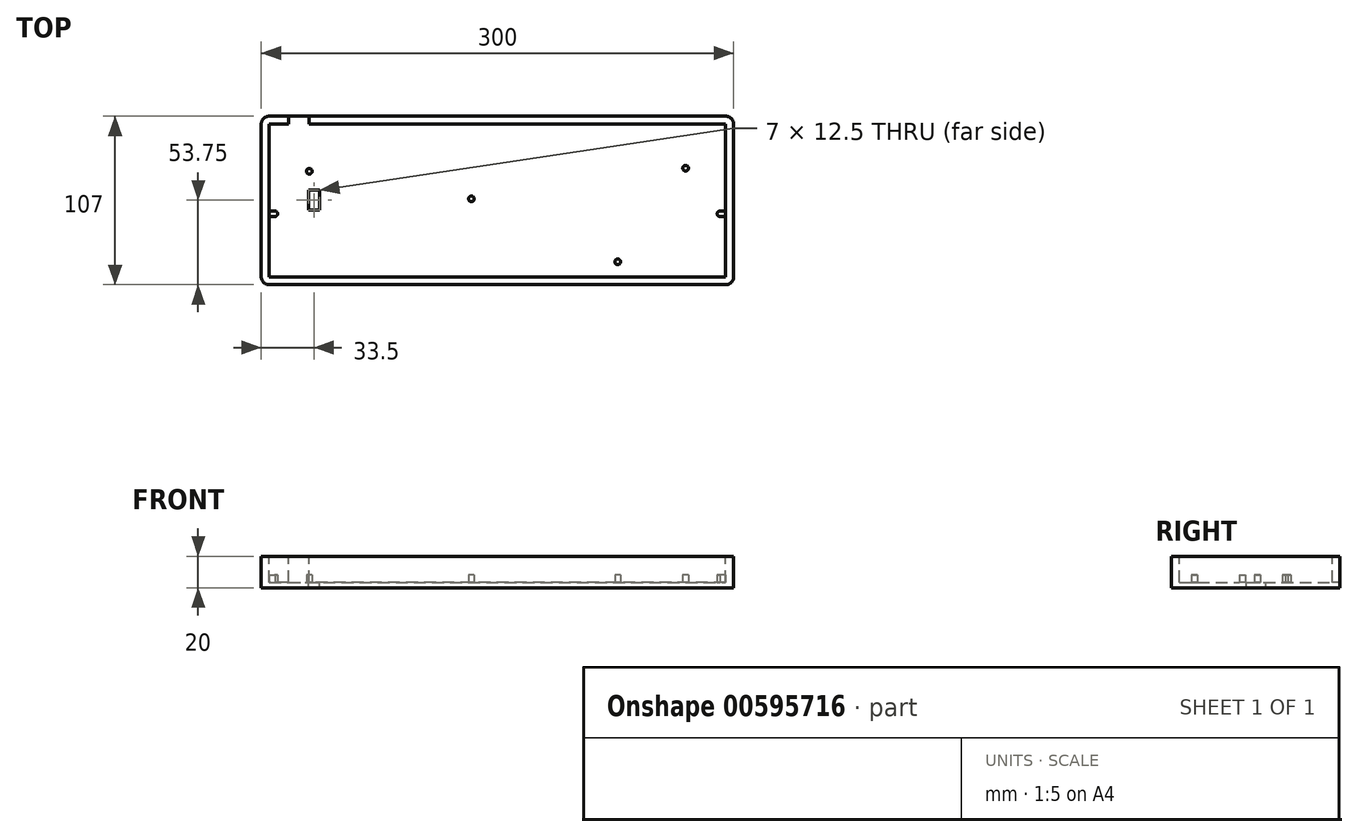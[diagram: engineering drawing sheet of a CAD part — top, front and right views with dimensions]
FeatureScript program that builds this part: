
annotation { "Feature Type Name" : "Feature", "Feature Type Description" : "" }
export const myFeature = defineFeature(function(context is Context, id is Id, definition is map)
    precondition{}
    {
        {
            var Q0;
            Q0=qCreatedBy(makeId("Top.planeOp"),FACE);
            var sketch = newSketch(context, id + "F0", { "sketchPlane" : qUnion([Q0])});
            skLineSegment(sketch, "E0.bottom", {"start": v(0, 0) * mm, "end": v(300, 0) * mm});
            skLineSegment(sketch, "E0.top", {"start": v(0, 107) * mm, "end": v(300, 107) * mm});
            skLineSegment(sketch, "E0.left", {"start": v(0, 0) * mm, "end": v(0, 107) * mm});
            skLineSegment(sketch, "E0.right", {"start": v(300, 0) * mm, "end": v(300, 107) * mm});
            skSolve(sketch);
        }
        {
            var Q0;
            Q0 = qSketchRegion(id + "F0", true);
            extrude(context, id + "F1", {"entities" : qUnion([Q0]), "depth" : 20 * mm, "offsetDistance" : 25 * mm});
        }
        {
            var Q0;
            Q0=makeQuery(id+"F1.opExtrude","SWEPT_EDGE",EDGE,{"disambiguationData":[OSD([sQuery(id+"F0.wireOp",EDGE,"E0.top"),sQuery(id+"F0.wireOp",EDGE,"E0.left")])]});
            var Q1;
            Q1=makeQuery(id+"F1.opExtrude","SWEPT_EDGE",EDGE,{"disambiguationData":[OSD([sQuery(id+"F0.wireOp",EDGE,"E0.bottom"),sQuery(id+"F0.wireOp",EDGE,"E0.left")])]});
            var Q2;
            Q2=makeQuery(id+"F1.opExtrude","SWEPT_EDGE",EDGE,{"disambiguationData":[OSD([sQuery(id+"F0.wireOp",EDGE,"E0.bottom"),sQuery(id+"F0.wireOp",EDGE,"E0.right")])]});
            var Q3;
            Q3=makeQuery(id+"F1.opExtrude","SWEPT_EDGE",EDGE,{"disambiguationData":[OSD([sQuery(id+"F0.wireOp",EDGE,"E0.top"),sQuery(id+"F0.wireOp",EDGE,"E0.right")])]});
            fillet(context, id + "F2", {"entities" : qUnion([Q0, Q1, Q2, Q3]), "radius" : 5 * mm, "tangentPropagation" : true, "allowEdgeOverflow" : false});
        }
        {
            var Q0;
            Q0=makeQuery(id+"F1.opExtrude","CAP_FACE",FACE,{"disambiguationData":[OSD([sQuery(id+"F0.wireOp",EDGE,"E0.bottom"),sQuery(id+"F0.wireOp",EDGE,"E0.top"),sQuery(id+"F0.wireOp",EDGE,"E0.left"),sQuery(id+"F0.wireOp",EDGE,"E0.right")])],"isStart":false});
            var sketch = newSketch(context, id + "F3", { "sketchPlane" : qUnion([Q0])});
            skLineSegment(sketch, "E1", {"start": v(5, 102) * mm, "end": v(5, 5) * mm});
            skLineSegment(sketch, "E2", {"start": v(5, 5) * mm, "end": v(295, 5) * mm});
            skLineSegment(sketch, "E3", {"start": v(295, 5) * mm, "end": v(295, 102) * mm});
            skLineSegment(sketch, "E4", {"start": v(295, 102) * mm, "end": v(5, 102) * mm});
            skLineSegment(sketch, "E5", {"start": v(17.5, 102) * mm, "end": v(17.5, 107) * mm});
            skLineSegment(sketch, "E6", {"start": v(17.5, 107) * mm, "end": v(30.5, 107) * mm});
            skLineSegment(sketch, "E7", {"start": v(30.5, 107) * mm, "end": v(30.5, 102) * mm});
            skSolve(sketch);
        }
        {
            var Q0;
            Q0 = qSketchRegion(id + "F3", true);
            var Q1;
            Q1=makeQuery(id+"F1.opExtrude","CAP_FACE",FACE,{"disambiguationData":[OSD([sQuery(id+"F0.wireOp",EDGE,"E0.bottom"),sQuery(id+"F0.wireOp",EDGE,"E0.top"),sQuery(id+"F0.wireOp",EDGE,"E0.left"),sQuery(id+"F0.wireOp",EDGE,"E0.right")])],"isStart":true});
            extrude(context, id + "F4", {"entities" : qUnion([Q0, Q1]), "operationType" : NewBodyOperationType.REMOVE, "oppositeDirection" : true, "depth" : 16.5 * mm, "offsetDistance" : 25 * mm});
        }
        {
            var Q0;
            Q0=makeQuery(id+"F4.boolean.opBoolean","COPY",FACE,{"derivedFrom":makeQuery(id+"F4.opExtrude","CAP_FACE",FACE,{"disambiguationData":[OSD([sQuery(id+"F3.wireOp",EDGE,"E1"),sQuery(id+"F3.wireOp",EDGE,"E2"),sQuery(id+"F3.wireOp",EDGE,"E3"),sQuery(id+"F3.wireOp",EDGE,"E4")])],"isStart":false})});
            var sketch = newSketch(context, id + "F5", { "sketchPlane" : qUnion([Q0])});
            skCircle(sketch, "E8", {"center": v(269.5, 74) * mm, "radius": 1.8 * mm});
            skCircle(sketch, "E9", {"center": v(226.42, 14.5) * mm, "radius": 1.8 * mm});
            skCircle(sketch, "E10", {"center": v(133.5, 54.5) * mm, "radius": 1.8 * mm});
            skCircle(sketch, "E11", {"center": v(30.5, 72) * mm, "radius": 1.8 * mm});
            skLineSegment(sketch, "E12", {"start": v(5, 46.8) * mm, "end": v(8.6, 46.8) * mm});
            skLineSegment(sketch, "E13", {"start": v(5, 43.2) * mm, "end": v(8.62, 43.2) * mm});
            skLineSegment(sketch, "E14", {"start": v(8.62, 43.2) * mm, "end": v(8.6, 46.8) * mm, "construction": true});
            skArc(sketch, "E15", {"start": v(8.62, 43.2) * mm, "mid": v(10.4, 45.01) * mm, "end": v(8.6, 46.8) * mm});
            skLineSegment(sketch, "E16", {"start": v(5, 22.63) * mm, "end": v(150, 22.63) * mm, "construction": true});
            skLineSegment(sketch, "E17", {"start": v(150, 22.63) * mm, "end": v(295, 22.63) * mm, "construction": true});
            skLineSegment(sketch, "E18", {"start": v(150, 22.63) * mm, "end": v(150, 102) * mm, "construction": true});
            skLineSegment(sketch, "E19.MirrorCS", {"start": v(295, 46.8) * mm, "end": v(291.4, 46.8) * mm});
            skLineSegment(sketch, "E20.MirrorCS", {"start": v(295, 43.2) * mm, "end": v(291.38, 43.2) * mm});
            skArc(sketch, "E21.MirrorCS", {"start": v(291.38, 43.2) * mm, "mid": v(289.6, 45.01) * mm, "end": v(291.4, 46.8) * mm});
            skLineSegment(sketch, "E22.MirrorCS", {"start": v(291.38, 43.2) * mm, "end": v(291.4, 46.8) * mm, "construction": true});
            skLineSegment(sketch, "E23", {"start": v(5, 46.8) * mm, "end": v(5, 43.2) * mm});
            skLineSegment(sketch, "E24", {"start": v(295, 46.8) * mm, "end": v(295, 43.2) * mm});
            skSolve(sketch);
        }
        {
            var Q0;
            Q0 = qSketchRegion(id + "F5", true);
            extrude(context, id + "F6", {"entities" : qUnion([Q0]), "operationType" : NewBodyOperationType.ADD, "depth" : 4.5 * mm, "offsetDistance" : 25 * mm});
        }
        {
            var Q0;
            Q0=makeQuery(id+"F4.boolean.opBoolean","COPY",FACE,{"derivedFrom":makeQuery(id+"F4.opExtrude","CAP_FACE",FACE,{"disambiguationData":[OSD([sQuery(id+"F3.wireOp",EDGE,"E1"),sQuery(id+"F3.wireOp",EDGE,"E2"),sQuery(id+"F3.wireOp",EDGE,"E3"),sQuery(id+"F3.wireOp",EDGE,"E4"),sQuery(id+"F3.wireOp",EDGE,"E5"),sQuery(id+"F3.wireOp",EDGE,"E6"),sQuery(id+"F3.wireOp",EDGE,"E7")])],"isStart":false})});
            var sketch = newSketch(context, id + "F7", { "sketchPlane" : qUnion([Q0])});
            skLineSegment(sketch, "E25.bottom", {"start": v(30, 47.5) * mm, "end": v(37, 47.5) * mm});
            skLineSegment(sketch, "E25.top", {"start": v(30, 60) * mm, "end": v(37, 60) * mm});
            skLineSegment(sketch, "E25.left", {"start": v(30, 47.5) * mm, "end": v(30, 60) * mm});
            skLineSegment(sketch, "E25.right", {"start": v(37, 47.5) * mm, "end": v(37, 60) * mm});
            skSolve(sketch);
        }
        {
            var Q0;
            Q0 = qSketchRegion(id + "F7", true);
            extrude(context, id + "F8", {"entities" : qUnion([Q0]), "operationType" : NewBodyOperationType.REMOVE, "oppositeDirection" : true, "depth" : 25 * mm, "offsetDistance" : 25 * mm});
        }
    });
